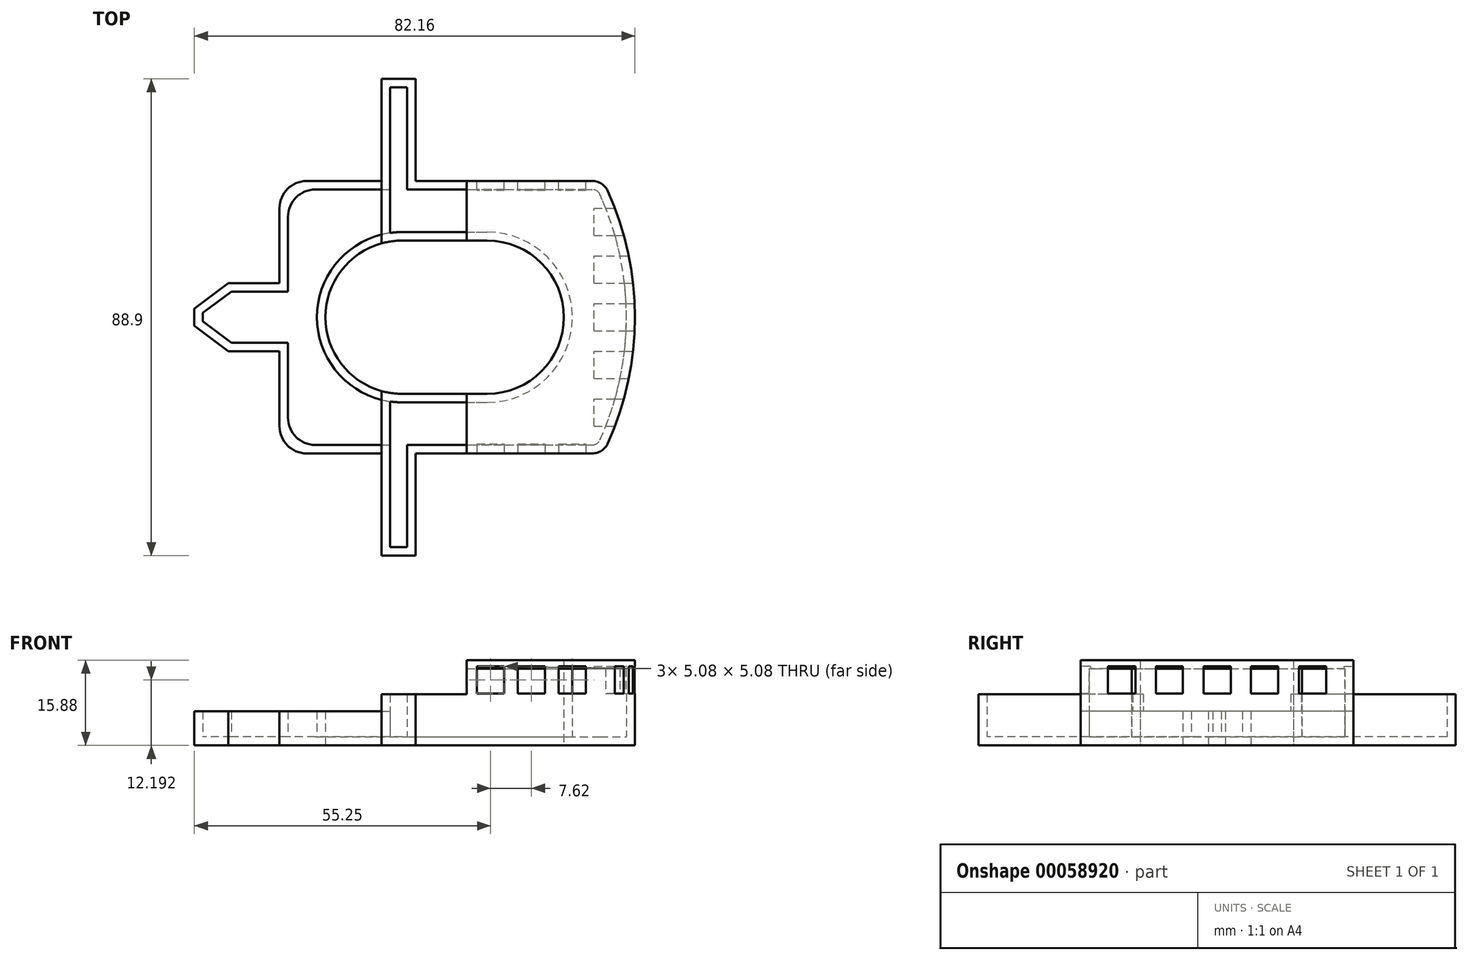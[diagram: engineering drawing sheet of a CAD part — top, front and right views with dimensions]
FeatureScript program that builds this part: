
annotation { "Feature Type Name" : "Feature", "Feature Type Description" : "" }
export const myFeature = defineFeature(function(context is Context, id is Id, definition is map)
    precondition{}
    {
        {
            var Q0;
            Q0=qCreatedBy(makeId("Top.planeOp"),FACE);
            var sketch = newSketch(context, id + "F0", { "sketchPlane" : qUnion([Q0])});
            skLineSegment(sketch, "E0.bottom", {"start": v(0, 50.8) * mm, "end": v(19.05, 50.8) * mm});
            skLineSegment(sketch, "E0.top", {"start": v(0, 0) * mm, "end": v(19.05, 0) * mm});
            skLineSegment(sketch, "E0.left", {"start": v(0, 50.8) * mm, "end": v(0, 0) * mm});
            skArc(sketch, "E1", {"start": v(61.2, 1.87) * mm, "mid": v(66.28, 25.4) * mm, "end": v(61.2, 48.93) * mm});
            skLineSegment(sketch, "E2.top", {"start": v(19.05, -19.05) * mm, "end": v(25.4, -19.05) * mm});
            skLineSegment(sketch, "E2.left", {"start": v(19.05, 0) * mm, "end": v(19.05, -19.05) * mm});
            skLineSegment(sketch, "E2.right", {"start": v(25.4, 0) * mm, "end": v(25.4, -19.05) * mm});
            skLineSegment(sketch, "E3.bottom", {"start": v(19.05, 69.85) * mm, "end": v(25.4, 69.85) * mm});
            skLineSegment(sketch, "E3.left", {"start": v(19.05, 69.85) * mm, "end": v(19.05, 50.8) * mm});
            skLineSegment(sketch, "E3.right", {"start": v(25.4, 69.85) * mm, "end": v(25.4, 50.8) * mm});
            skLineSegment(sketch, "E4.trimOffspring", {"start": v(25.4, 0) * mm, "end": v(58.32, 0) * mm});
            skLineSegment(sketch, "E5.trimOffspring", {"start": v(25.4, 50.8) * mm, "end": v(58.32, 50.8) * mm});
            skPoint(sketch, "E6.visualSharp", {"position": v(60.33, 50.8) * mm});
            skArc(sketch, "E6.filletArc", {"start": v(61.2, 48.93) * mm, "mid": v(60.04, 50.3) * mm, "end": v(58.32, 50.8) * mm});
            skPoint(sketch, "E7.visualSharp", {"position": v(60.33, 0) * mm});
            skArc(sketch, "E7.filletArc", {"start": v(58.32, 0) * mm, "mid": v(60.04, 0.5) * mm, "end": v(61.2, 1.87) * mm});
            skArc(sketch, "E8", {"start": v(22.86, 39.69) * mm, "mid": v(8.57, 25.4) * mm, "end": v(22.86, 11.11) * mm});
            skArc(sketch, "E9", {"start": v(38.74, 11.11) * mm, "mid": v(53.02, 25.4) * mm, "end": v(38.74, 39.69) * mm});
            skLineSegment(sketch, "E10", {"start": v(22.86, 39.69) * mm, "end": v(38.74, 39.69) * mm});
            skLineSegment(sketch, "E11", {"start": v(22.86, 11.11) * mm, "end": v(38.74, 11.11) * mm});
            skLineSegment(sketch, "E12", {"start": v(0, 31.75) * mm, "end": v(-9.53, 31.75) * mm});
            skLineSegment(sketch, "E13", {"start": v(-9.53, 31.75) * mm, "end": v(-15.88, 26.99) * mm});
            skLineSegment(sketch, "E14", {"start": v(-15.88, 26.99) * mm, "end": v(-15.88, 23.81) * mm});
            skLineSegment(sketch, "E15", {"start": v(-15.88, 23.81) * mm, "end": v(-9.52, 19.05) * mm});
            skLineSegment(sketch, "E16", {"start": v(-9.53, 19.05) * mm, "end": v(0, 19.05) * mm});
            skLineSegment(sketch, "E17", {"start": v(0, 19.05) * mm, "end": v(0, 31.75) * mm});
            skLineSegment(sketch, "E18", {"start": v(34.92, 50.8) * mm, "end": v(34.92, 39.69) * mm});
            skLineSegment(sketch, "E19", {"start": v(19.05, 50.8) * mm, "end": v(19.05, 39.17) * mm});
            skLineSegment(sketch, "E20.trimOffspring", {"start": v(19.05, 11.63) * mm, "end": v(19.05, 0) * mm});
            skLineSegment(sketch, "E21.trimOffspring", {"start": v(34.92, 11.11) * mm, "end": v(34.92, 0) * mm});
            skSolve(sketch);
        }
        {
            var Q0;
            Q0=makeQuery(id+"F0.imprint","IMPRINT",FACE,{"disambiguationData":[TD([[makeQuery(id+"F0.imprint","IMPRINT",EDGE,{"derivedFrom":sQuery(id+"F0.wireOp",EDGE,"E1")}),1.0]])]});
            extrude(context, id + "F1", {"entities" : qUnion([Q0]), "depth" : 15.88 * mm});
        }
        {
            var Q0;
            Q0=makeQuery(id+"F0.imprint","IMPRINT",FACE,{"disambiguationData":[TD([[makeQuery(id+"F0.imprint","IMPRINT",EDGE,{"derivedFrom":sQuery(id+"F0.wireOp",EDGE,"E3.bottom")}),-1.0]])]});
            var Q1;
            Q1=makeQuery(id+"F0.imprint","IMPRINT",FACE,{"disambiguationData":[TD([[makeQuery(id+"F0.imprint","IMPRINT",EDGE,{"derivedFrom":sQuery(id+"F0.wireOp",EDGE,"E2.top")}),1.0]])]});
            extrude(context, id + "F2", {"entities" : qUnion([Q0, Q1]), "operationType" : NewBodyOperationType.ADD, "depth" : 9.52 * mm});
        }
        {
            var Q0;
            {var subQ3=sQuery(id+"F0.wireOp",EDGE,"E0.bottom");Q0=makeQuery(id+"F0.imprint","IMPRINT",FACE,{"disambiguationData":[TD([[makeQuery(id+"F0.imprint","IMPRINT",EDGE,{"derivedFrom":subQ3}),-1.0]])]});}
            var Q1;
            Q1=makeQuery(id+"F0.imprint","IMPRINT",FACE,{"disambiguationData":[TD([[makeQuery(id+"F0.imprint","IMPRINT",EDGE,{"derivedFrom":sQuery(id+"F0.wireOp",EDGE,"E12")}),1.0]])]});
            extrude(context, id + "F3", {"entities" : qUnion([Q0, Q1]), "operationType" : NewBodyOperationType.ADD, "depth" : 6.35 * mm});
        }
        {
            var Q0;
            Q0=makeQuery(id+"F3.opExtrude","CAP_FACE",FACE,{"disambiguationData":[OSD([sQuery(id+"F0.wireOp",EDGE,"E0.bottom"),sQuery(id+"F0.wireOp",EDGE,"E0.top"),sQuery(id+"F0.wireOp",EDGE,"E0.left"),sQuery(id+"F0.wireOp",EDGE,"E8"),sQuery(id+"F0.wireOp",EDGE,"E12"),sQuery(id+"F0.wireOp",EDGE,"E13"),sQuery(id+"F0.wireOp",EDGE,"E14"),sQuery(id+"F0.wireOp",EDGE,"E15"),sQuery(id+"F0.wireOp",EDGE,"E16"),sQuery(id+"F0.wireOp",EDGE,"E19"),sQuery(id+"F0.wireOp",EDGE,"E20.trimOffspring")])],"isStart":false});
            var Q1;
            Q1=makeQuery(id+"F2.opExtrude","CAP_FACE",FACE,{"disambiguationData":[OSD([sQuery(id+"F0.wireOp",EDGE,"E3.bottom"),sQuery(id+"F0.wireOp",EDGE,"E3.left"),sQuery(id+"F0.wireOp",EDGE,"E3.right"),sQuery(id+"F0.wireOp",EDGE,"E5.trimOffspring"),sQuery(id+"F0.wireOp",EDGE,"E8"),sQuery(id+"F0.wireOp",EDGE,"E10"),sQuery(id+"F0.wireOp",EDGE,"E18"),sQuery(id+"F0.wireOp",EDGE,"E19")])],"isStart":false});
            var Q2;
            Q2=makeQuery(id+"F1.opExtrude","SWEPT_FACE",FACE,{"disambiguationData":[OSD([sQuery(id+"F0.wireOp",EDGE,"E21.trimOffspring")])]});
            var Q3;
            Q3=makeQuery(id+"F1.opExtrude","SWEPT_FACE",FACE,{"disambiguationData":[OSD([sQuery(id+"F0.wireOp",EDGE,"E18")])]});
            var Q4;
            Q4=makeQuery(id+"F2.opExtrude","CAP_FACE",FACE,{"disambiguationData":[OSD([sQuery(id+"F0.wireOp",EDGE,"E2.top"),sQuery(id+"F0.wireOp",EDGE,"E2.left"),sQuery(id+"F0.wireOp",EDGE,"E2.right"),sQuery(id+"F0.wireOp",EDGE,"E4.trimOffspring"),sQuery(id+"F0.wireOp",EDGE,"E8"),sQuery(id+"F0.wireOp",EDGE,"E11"),sQuery(id+"F0.wireOp",EDGE,"E20.trimOffspring"),sQuery(id+"F0.wireOp",EDGE,"E21.trimOffspring")])],"isStart":false});
            shell(context, id + "F4", {"entities" : qUnion([Q0, Q1, Q2, Q3, Q4]), "thickness" : 1.59 * mm});
        }
        {
            var Q0;
            {var subQ0=sQuery(id+"F0.wireOp",EDGE,"E5.trimOffspring");Q0=makeQuery(id+"F2.boolean.opBoolean","MERGE",FACE,{"derivedFrom":[makeQuery(id+"F1.opExtrude","SWEPT_FACE",FACE,{"disambiguationData":[OSD([subQ0])]}),makeQuery(id+"F2.opExtrude","SWEPT_FACE",FACE,{"disambiguationData":[OSD([subQ0])]})]});}
            var sketch = newSketch(context, id + "F5", { "sketchPlane" : qUnion([Q0])});
            skLineSegment(sketch, "E22.bottom", {"start": v(-57.15, 14.73) * mm, "end": v(-52.07, 14.73) * mm});
            skLineSegment(sketch, "E22.top", {"start": v(-57.15, 9.65) * mm, "end": v(-52.07, 9.65) * mm});
            skLineSegment(sketch, "E22.left", {"start": v(-57.15, 14.73) * mm, "end": v(-57.15, 9.65) * mm});
            skLineSegment(sketch, "E22.right", {"start": v(-52.07, 14.73) * mm, "end": v(-52.07, 9.65) * mm});
            skLineSegment(sketch, "E23.left", {"start": v(-49.53, 14.73) * mm, "end": v(-49.53, 9.65) * mm});
            skLineSegment(sketch, "E23.bottom", {"start": v(-49.53, 14.73) * mm, "end": v(-44.45, 14.73) * mm});
            skLineSegment(sketch, "E23.top", {"start": v(-49.53, 9.65) * mm, "end": v(-44.45, 9.65) * mm});
            skLineSegment(sketch, "E23.right", {"start": v(-44.45, 14.73) * mm, "end": v(-44.45, 9.65) * mm});
            skLineSegment(sketch, "E24.left", {"start": v(-41.9, 14.73) * mm, "end": v(-41.9, 9.65) * mm});
            skLineSegment(sketch, "E24.bottom", {"start": v(-41.9, 14.73) * mm, "end": v(-36.83, 14.73) * mm});
            skLineSegment(sketch, "E24.top", {"start": v(-41.9, 9.65) * mm, "end": v(-36.83, 9.65) * mm});
            skLineSegment(sketch, "E24.right", {"start": v(-36.83, 14.73) * mm, "end": v(-36.83, 9.65) * mm});
            skSolve(sketch);
        }
        {
            var Q0;
            Q0 = qSketchRegion(id + "F5", true);
            extrude(context, id + "F6", {"entities" : qUnion([Q0]), "operationType" : NewBodyOperationType.REMOVE, "oppositeDirection" : true, "depth" : 1.78 * mm});
        }
        {
            var Q0;
            {var subQ0=sQuery(id+"F0.wireOp",EDGE,"E4.trimOffspring");Q0=makeQuery(id+"F2.boolean.opBoolean","MERGE",FACE,{"derivedFrom":[makeQuery(id+"F1.opExtrude","SWEPT_FACE",FACE,{"disambiguationData":[OSD([subQ0])]}),makeQuery(id+"F2.opExtrude","SWEPT_FACE",FACE,{"disambiguationData":[OSD([subQ0])]})]});}
            var sketch = newSketch(context, id + "F7", { "sketchPlane" : qUnion([Q0])});
            skLineSegment(sketch, "E25.right", {"start": v(57.15, 14.73) * mm, "end": v(57.15, 9.65) * mm});
            skLineSegment(sketch, "E26.bottom", {"start": v(36.83, 14.73) * mm, "end": v(41.9, 14.73) * mm});
            skLineSegment(sketch, "E25.top", {"start": v(52.07, 9.65) * mm, "end": v(57.15, 9.65) * mm});
            skLineSegment(sketch, "E25.bottom", {"start": v(52.07, 14.73) * mm, "end": v(57.15, 14.73) * mm});
            skLineSegment(sketch, "E27.right", {"start": v(49.53, 14.73) * mm, "end": v(49.53, 9.65) * mm});
            skLineSegment(sketch, "E27.top", {"start": v(44.45, 9.65) * mm, "end": v(49.53, 9.65) * mm});
            skLineSegment(sketch, "E27.bottom", {"start": v(44.45, 14.73) * mm, "end": v(49.53, 14.73) * mm});
            skLineSegment(sketch, "E27.left", {"start": v(44.45, 14.73) * mm, "end": v(44.45, 9.65) * mm});
            skLineSegment(sketch, "E26.right", {"start": v(41.9, 14.73) * mm, "end": v(41.9, 9.65) * mm});
            skLineSegment(sketch, "E26.left", {"start": v(36.83, 14.73) * mm, "end": v(36.83, 9.65) * mm});
            skLineSegment(sketch, "E26.top", {"start": v(36.83, 9.65) * mm, "end": v(41.9, 9.65) * mm});
            skLineSegment(sketch, "E25.left", {"start": v(52.07, 14.73) * mm, "end": v(52.07, 9.65) * mm});
            skSolve(sketch);
        }
        {
            var Q0;
            Q0=makeQuery(id+"F7.imprint","IMPRINT",FACE,{"disambiguationData":[TD([[makeQuery(id+"F7.imprint","IMPRINT",EDGE,{"derivedFrom":sQuery(id+"F7.wireOp",EDGE,"E26.bottom")}),-1.0]])]});
            var Q1;
            Q1=makeQuery(id+"F7.imprint","IMPRINT",FACE,{"disambiguationData":[TD([[makeQuery(id+"F7.imprint","IMPRINT",EDGE,{"derivedFrom":sQuery(id+"F7.wireOp",EDGE,"E27.right")}),-1.0]])]});
            var Q2;
            Q2=makeQuery(id+"F7.imprint","IMPRINT",FACE,{"disambiguationData":[TD([[makeQuery(id+"F7.imprint","IMPRINT",EDGE,{"derivedFrom":sQuery(id+"F7.wireOp",EDGE,"E25.right")}),-1.0]])]});
            extrude(context, id + "F8", {"entities" : qUnion([Q0, Q1, Q2]), "operationType" : NewBodyOperationType.REMOVE, "oppositeDirection" : true, "depth" : 1.78 * mm});
        }
        {
            var Q0;
            Q0=qCreatedBy(makeId("Right.planeOp"),FACE);
            cPlane(context, id + "F9", {"entities" : qUnion([Q0]), "cplaneType" : CPlaneType.OFFSET, "offset" : 66.3 * mm, "width" : 152.4 * mm, "height" : 152.4 * mm});
        }
        {
            var Q0;
            Q0=qCreatedBy(id+"F9.planeOp",FACE);
            var sketch = newSketch(context, id + "F10", { "sketchPlane" : qUnion([Q0])});
            skLineSegment(sketch, "E28.bottom", {"start": v(5.08, 14.73) * mm, "end": v(10.16, 14.73) * mm});
            skLineSegment(sketch, "E28.top", {"start": v(5.08, 9.65) * mm, "end": v(10.16, 9.65) * mm});
            skLineSegment(sketch, "E28.left", {"start": v(5.08, 14.73) * mm, "end": v(5.08, 9.65) * mm});
            skLineSegment(sketch, "E28.right", {"start": v(10.16, 14.73) * mm, "end": v(10.16, 9.65) * mm});
            skLineSegment(sketch, "E29.1.0.0", {"start": v(19.05, 14.73) * mm, "end": v(19.05, 9.65) * mm});
            skLineSegment(sketch, "E29.1.0.1", {"start": v(13.97, 14.73) * mm, "end": v(13.97, 9.65) * mm});
            skLineSegment(sketch, "E29.1.0.2", {"start": v(13.97, 9.65) * mm, "end": v(19.05, 9.65) * mm});
            skLineSegment(sketch, "E29.1.0.3", {"start": v(13.97, 14.73) * mm, "end": v(19.05, 14.73) * mm});
            skLineSegment(sketch, "E29.2.0.0", {"start": v(27.94, 14.73) * mm, "end": v(27.94, 9.65) * mm});
            skLineSegment(sketch, "E29.2.0.1", {"start": v(22.86, 14.73) * mm, "end": v(22.86, 9.65) * mm});
            skLineSegment(sketch, "E29.2.0.2", {"start": v(22.86, 9.65) * mm, "end": v(27.94, 9.65) * mm});
            skLineSegment(sketch, "E29.2.0.3", {"start": v(22.86, 14.73) * mm, "end": v(27.94, 14.73) * mm});
            skLineSegment(sketch, "E29.3.0.0", {"start": v(36.83, 14.73) * mm, "end": v(36.83, 9.65) * mm});
            skLineSegment(sketch, "E29.3.0.1", {"start": v(31.75, 14.73) * mm, "end": v(31.75, 9.65) * mm});
            skLineSegment(sketch, "E29.3.0.2", {"start": v(31.75, 9.65) * mm, "end": v(36.83, 9.65) * mm});
            skLineSegment(sketch, "E29.3.0.3", {"start": v(31.75, 14.73) * mm, "end": v(36.83, 14.73) * mm});
            skLineSegment(sketch, "E29.4.0.0", {"start": v(45.72, 14.73) * mm, "end": v(45.72, 9.65) * mm});
            skLineSegment(sketch, "E29.4.0.1", {"start": v(40.64, 14.73) * mm, "end": v(40.64, 9.65) * mm});
            skLineSegment(sketch, "E29.4.0.2", {"start": v(40.64, 9.65) * mm, "end": v(45.72, 9.65) * mm});
            skLineSegment(sketch, "E29.4.0.3", {"start": v(40.64, 14.73) * mm, "end": v(45.72, 14.73) * mm});
            skLineSegment(sketch, "E29.direction1", {"start": v(10.16, 9.65) * mm, "end": v(19.05, 9.65) * mm, "construction": true});
            skSolve(sketch);
        }
        {
            var Q0;
            Q0=makeQuery(id+"F10.imprint","IMPRINT",FACE,{"disambiguationData":[TD([[makeQuery(id+"F10.imprint","IMPRINT",EDGE,{"derivedFrom":sQuery(id+"F10.wireOp",EDGE,"E28.bottom")}),-1.0]])]});
            extrude(context, id + "F11", {"entities" : qUnion([Q0]), "operationType" : NewBodyOperationType.REMOVE, "oppositeDirection" : true, "depth" : 7.62 * mm});
        }
        {
            var Q0;
            Q0=makeQuery(id+"F10.imprint","IMPRINT",FACE,{"disambiguationData":[TD([[makeQuery(id+"F10.imprint","IMPRINT",EDGE,{"derivedFrom":sQuery(id+"F10.wireOp",EDGE,"E29.1.0.0")}),-1.0]])]});
            var Q1;
            Q1=makeQuery(id+"F10.imprint","IMPRINT",FACE,{"disambiguationData":[TD([[makeQuery(id+"F10.imprint","IMPRINT",EDGE,{"derivedFrom":sQuery(id+"F10.wireOp",EDGE,"E29.2.0.0")}),-1.0]])]});
            var Q2;
            Q2=makeQuery(id+"F10.imprint","IMPRINT",FACE,{"disambiguationData":[TD([[makeQuery(id+"F10.imprint","IMPRINT",EDGE,{"derivedFrom":sQuery(id+"F10.wireOp",EDGE,"E29.3.0.0")}),-1.0]])]});
            var Q3;
            Q3=makeQuery(id+"F10.imprint","IMPRINT",FACE,{"disambiguationData":[TD([[makeQuery(id+"F10.imprint","IMPRINT",EDGE,{"derivedFrom":sQuery(id+"F10.wireOp",EDGE,"E29.4.0.0")}),-1.0]])]});
            extrude(context, id + "F12", {"entities" : qUnion([Q0, Q1, Q2, Q3]), "operationType" : NewBodyOperationType.REMOVE, "oppositeDirection" : true, "depth" : 7.62 * mm});
        }
        {
            var Q0;
            Q0=makeQuery(id+"F3.opExtrude","SWEPT_EDGE",EDGE,{"disambiguationData":[OSD([sQuery(id+"F0.wireOp",EDGE,"E0.top"),sQuery(id+"F0.wireOp",EDGE,"E0.left")])]});
            var Q1;
            Q1=makeQuery(id+"F4.opShell","OFFSET_EDGE",EDGE,{"disambiguationData":[OSD([sQuery(id+"F0.wireOp",EDGE,"E0.top"),sQuery(id+"F0.wireOp",EDGE,"E0.left")])]});
            var Q2;
            Q2=makeQuery(id+"F3.opExtrude","SWEPT_EDGE",EDGE,{"disambiguationData":[OSD([sQuery(id+"F0.wireOp",EDGE,"E0.bottom"),sQuery(id+"F0.wireOp",EDGE,"E0.left")])]});
            var Q3;
            Q3=makeQuery(id+"F4.opShell","OFFSET_EDGE",EDGE,{"disambiguationData":[OSD([sQuery(id+"F0.wireOp",EDGE,"E0.bottom"),sQuery(id+"F0.wireOp",EDGE,"E0.left")])]});
            fillet(context, id + "F13", {"entities" : qUnion([Q0, Q1, Q2, Q3]), "radius" : 5.08 * mm, "tangentPropagation" : true, "allowEdgeOverflow" : false});
        }
    });
